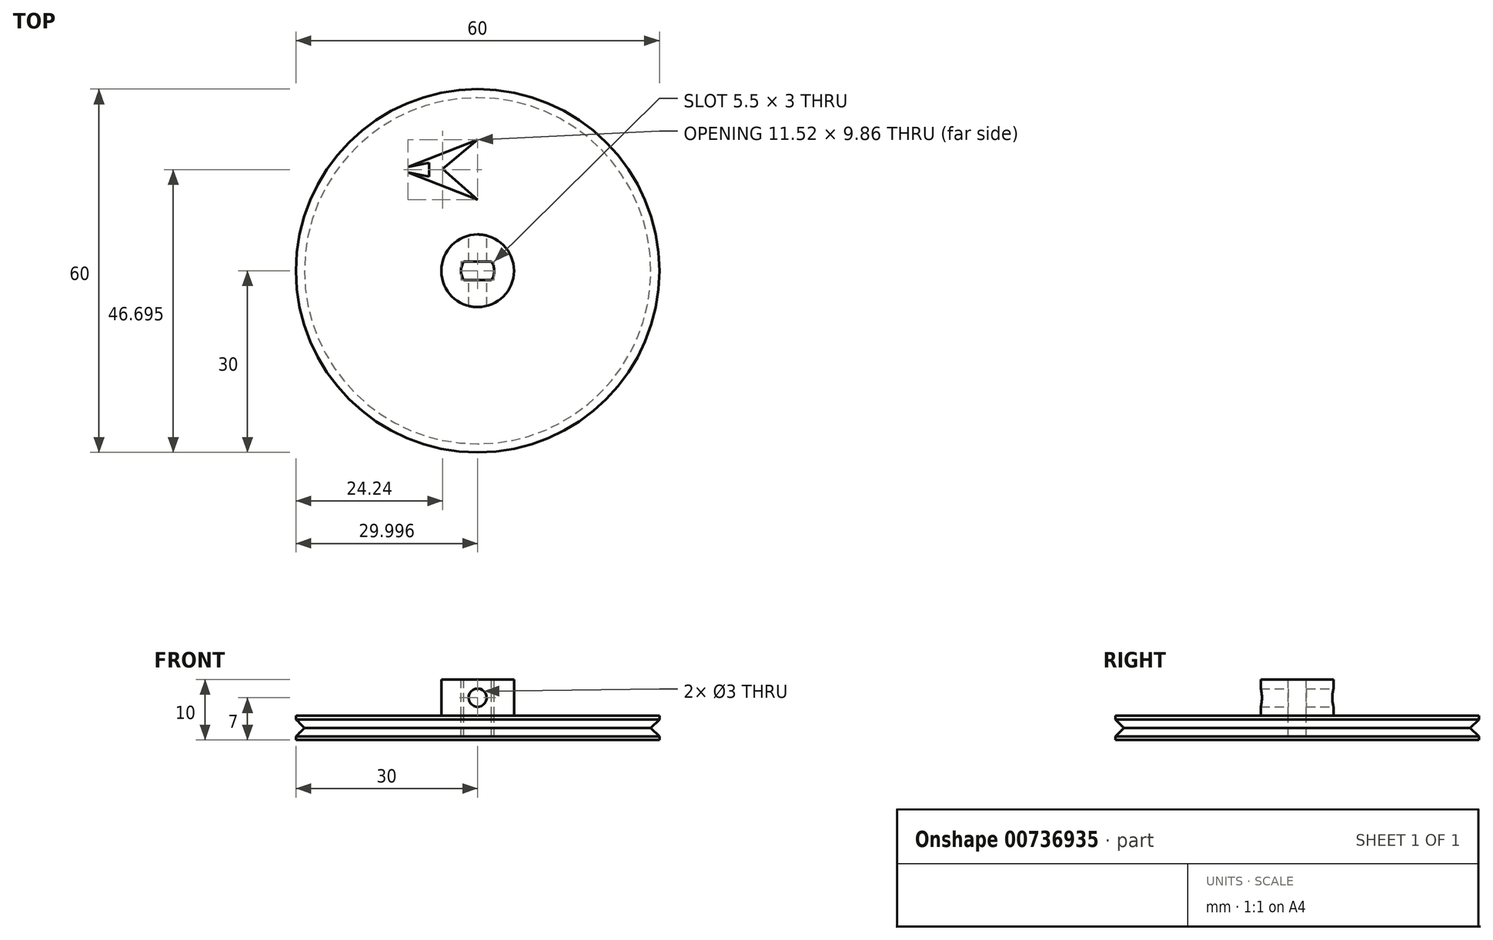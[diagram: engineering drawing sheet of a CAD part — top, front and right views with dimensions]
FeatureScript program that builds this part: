
annotation { "Feature Type Name" : "Feature", "Feature Type Description" : "" }
export const myFeature = defineFeature(function(context is Context, id is Id, definition is map)
    precondition{}
    {
        {
            var Q0;
            Q0=qCreatedBy(makeId("Top.planeOp"),FACE);
            var sketch = newSketch(context, id + "F0", { "sketchPlane" : qUnion([Q0])});
            skCircle(sketch, "E0", {"center": v(0, 0) * mm, "radius": 30 * mm});
            skCircle(sketch, "E1", {"center": v(0, 0) * mm, "radius": 6 * mm});
            skSolve(sketch);
        }
        {
            var Q0;
            Q0=makeQuery(id+"F0.imprint","IMPRINT",FACE,{"disambiguationData":[TD([[makeQuery(id+"F0.imprint","IMPRINT",EDGE,{"derivedFrom":sQuery(id+"F0.wireOp",EDGE,"E0")}),1.0]])]});
            var Q1;
            Q1=makeQuery(id+"F0.imprint","IMPRINT",FACE,{"disambiguationData":[TD([[makeQuery(id+"F0.imprint","IMPRINT",EDGE,{"derivedFrom":sQuery(id+"F0.wireOp",EDGE,"E1")}),1.0]])]});
            extrude(context, id + "F1", {"entities" : qUnion([Q0, Q1]), "oppositeDirection" : true, "depth" : 4 * mm, "offsetDistance" : 25 * mm});
        }
        {
            var Q0;
            Q0=makeQuery(id+"F0.imprint","IMPRINT",FACE,{"disambiguationData":[TD([[makeQuery(id+"F0.imprint","IMPRINT",EDGE,{"derivedFrom":sQuery(id+"F0.wireOp",EDGE,"E1")}),1.0]])]});
            extrude(context, id + "F2", {"entities" : qUnion([Q0]), "depth" : 6 * mm, "offsetDistance" : 25 * mm});
        }
        {
            var Q0;
            Q0=qCreatedBy(makeId("Front.planeOp"),FACE);
            var sketch = newSketch(context, id + "F3", { "sketchPlane" : qUnion([Q0])});
            skCircle(sketch, "E2", {"center": v(0, 3) * mm, "radius": 1.5 * mm});
            skSolve(sketch);
        }
        {
            var Q0;
            Q0 = qSketchRegion(id + "F3", true);
            extrude(context, id + "F4", {"entities" : qUnion([Q0]), "operationType" : NewBodyOperationType.REMOVE, "endBound" : BoundingType.SYMMETRIC, "depth" : 15 * mm, "offsetDistance" : 25 * mm});
        }
        {
            var Q0;
            Q0=makeQuery(id+"F2.opExtrude","CAP_FACE",FACE,{"disambiguationData":[OSD([sQuery(id+"F0.wireOp",EDGE,"E1")])],"isStart":false});
            var sketch = newSketch(context, id + "F5", { "sketchPlane" : qUnion([Q0])});
            skLineSegment(sketch, "E3.bottom", {"start": v(2.3, -1.5) * mm, "end": v(-2.3, -1.5) * mm});
            skLineSegment(sketch, "E3.top", {"start": v(2.3, 1.5) * mm, "end": v(-2.3, 1.5) * mm});
            skLineSegment(sketch, "E3.left", {"start": v(2.3, -1.5) * mm, "end": v(2.3, 1.5) * mm});
            skLineSegment(sketch, "E3.right", {"start": v(-2.3, -1.5) * mm, "end": v(-2.3, 1.5) * mm});
            skPoint(sketch, "E3.middle", {"position": v(0, 0) * mm});
            skArc(sketch, "E4", {"start": v(-2.3, 1.5) * mm, "mid": v(-2.75, 0) * mm, "end": v(-2.3, -1.5) * mm});
            skArc(sketch, "E5", {"start": v(2.3, -1.5) * mm, "mid": v(2.75, 0) * mm, "end": v(2.3, 1.5) * mm});
            skSolve(sketch);
        }
        {
            var Q0;
            Q0 = qSketchRegion(id + "F5", true);
            extrude(context, id + "F6", {"entities" : qUnion([Q0]), "operationType" : NewBodyOperationType.REMOVE, "oppositeDirection" : true, "depth" : 9.4 * mm, "offsetDistance" : 25 * mm});
        }
        {
            var Q0;
            Q0=qCreatedBy(makeId("Front.planeOp"),FACE);
            var sketch = newSketch(context, id + "F7", { "sketchPlane" : qUnion([Q0])});
            skLineSegment(sketch, "E6", {"start": v(-30, -4) * mm, "end": v(-30, 0) * mm, "construction": true});
            skLineSegment(sketch, "E7", {"start": v(-30, -0.59) * mm, "end": v(-28.59, -2) * mm});
            skLineSegment(sketch, "E8", {"start": v(-28.59, -2) * mm, "end": v(-30, -3.41) * mm});
            skLineSegment(sketch, "E9", {"start": v(-30, -2) * mm, "end": v(-26.31, -2) * mm, "construction": true});
            skLineSegment(sketch, "E10", {"start": v(0, 32.97) * mm, "end": v(0, -21.96) * mm, "construction": true});
            skLineSegment(sketch, "E11", {"start": v(-30, -0.59) * mm, "end": v(-30, -3.41) * mm});
            skSolve(sketch);
        }
        {
            var Q0;
            Q0 = qSketchRegion(id + "F7", true);
            var Q1;
            Q1=sQuery(id+"F7.wireOp",EDGE,"E10");
            revolve(context, id + "F8", {"operationType" : NewBodyOperationType.REMOVE, "surfaceOperationType" : NewSurfaceOperationType.NEW, "entities" : qUnion([Q0]), "axis" : qUnion([Q1]), "revolveType" : RevolveType.FULL, "oppositeDirection" : true});
        }
        {
            var Q0;
            Q0=makeQuery(id+"F0.imprint","IMPRINT",FACE,{"disambiguationData":[TD([[makeQuery(id+"F0.imprint","IMPRINT",EDGE,{"derivedFrom":sQuery(id+"F0.wireOp",EDGE,"E0")}),1.0]])]});
            var sketch = newSketch(context, id + "F9", { "sketchPlane" : qUnion([Q0])});
            skLineSegment(sketch, "E12", {"start": v(0, 73.06) * mm, "end": v(0, -57.38) * mm, "construction": true});
            skLineSegment(sketch, "E13", {"start": v(0, 21.62) * mm, "end": v(-11.5, 17.11) * mm});
            skLineSegment(sketch, "E14", {"start": v(0, 11.77) * mm, "end": v(-11.52, 16.23) * mm});
            skLineSegment(sketch, "E15", {"start": v(0, 21.62) * mm, "end": v(-5.82, 16.85) * mm});
            skLineSegment(sketch, "E16", {"start": v(-5.82, 16.85) * mm, "end": v(0, 11.77) * mm});
            skLineSegment(sketch, "E17", {"start": v(-11.5, 17.11) * mm, "end": v(-8.02, 17.87) * mm});
            skLineSegment(sketch, "E18", {"start": v(-8.02, 17.87) * mm, "end": v(-8.02, 15.56) * mm});
            skLineSegment(sketch, "E19", {"start": v(-8.02, 15.56) * mm, "end": v(-11.52, 16.23) * mm});
            skLineSegment(sketch, "E20", {"start": v(-47.62, 0) * mm, "end": v(37.49, 0) * mm, "construction": true});
            skSolve(sketch);
        }
        {
            var Q0;
            Q0 = qSketchRegion(id + "F9", true);
            var Q1;
            Q1=makeQuery(id+"F1.opExtrude","CAP_FACE",FACE,{"disambiguationData":[OSD([sQuery(id+"F0.wireOp",EDGE,"E0")])],"isStart":false});
            extrude(context, id + "F10", {"entities" : qUnion([Q0]), "operationType" : NewBodyOperationType.REMOVE, "endBound" : BoundingType.UP_TO_SURFACE, "oppositeDirection" : true, "depth" : 25 * mm, "endBoundEntityFace" : qUnion([Q1]), "offsetDistance" : 25 * mm});
        }
    });
